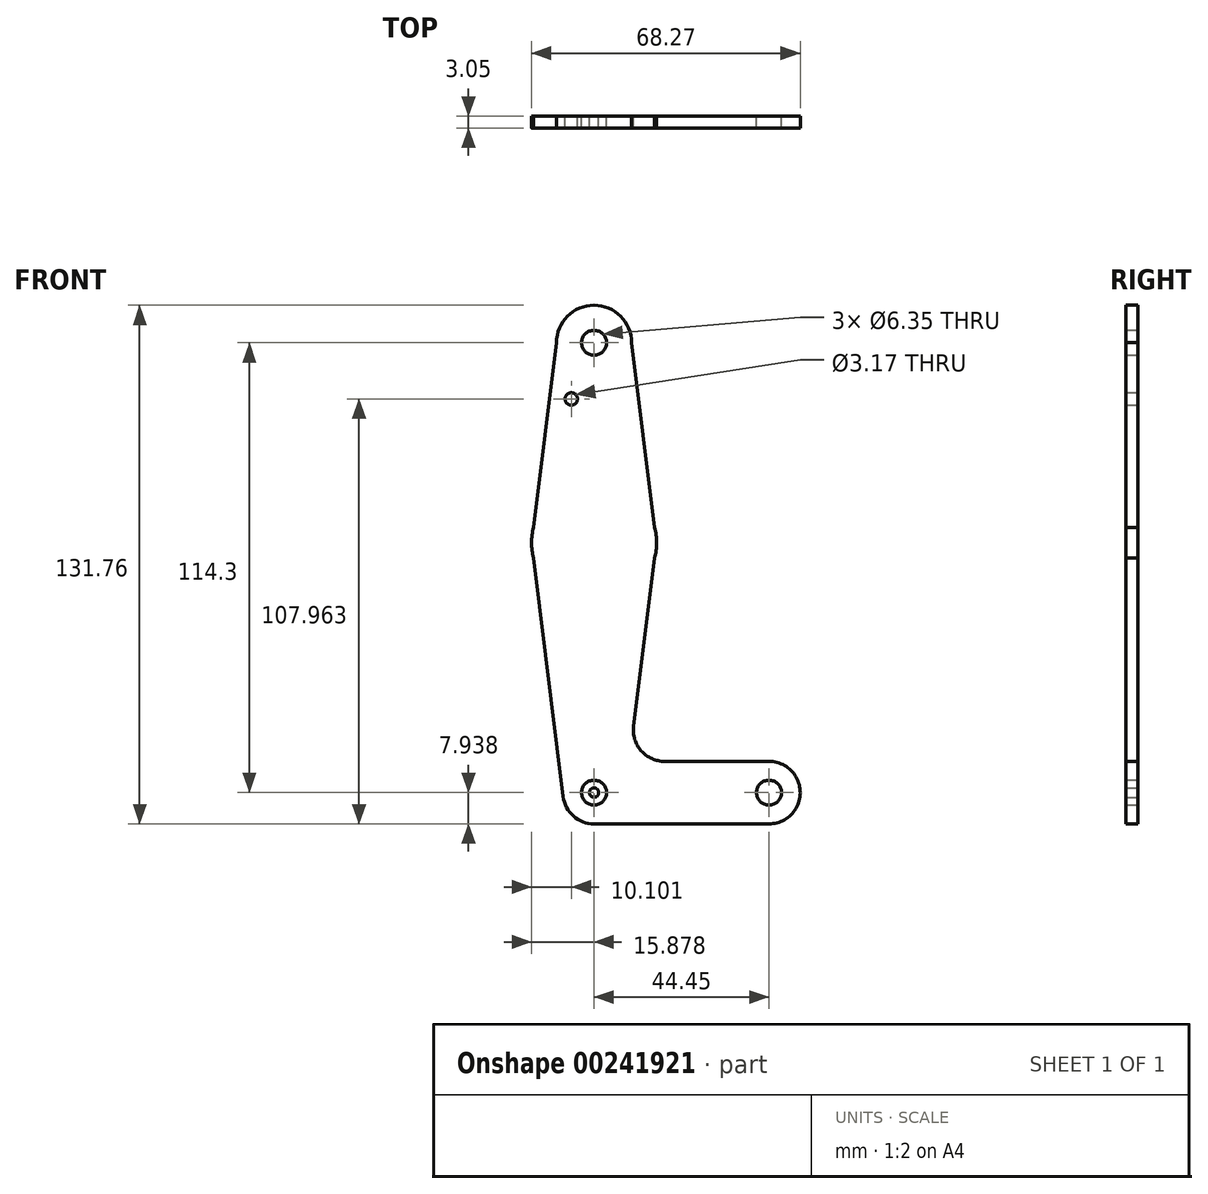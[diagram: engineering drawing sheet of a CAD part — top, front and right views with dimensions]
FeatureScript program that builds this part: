
annotation { "Feature Type Name" : "Feature", "Feature Type Description" : "" }
export const myFeature = defineFeature(function(context is Context, id is Id, definition is map)
    precondition{}
    {
        {
            var Q0;
            Q0=qCreatedBy(makeId("Front.planeOp"),FACE);
            var sketch = newSketch(context, id + "F0", { "sketchPlane" : qUnion([Q0])});
            skCircle(sketch, "E0", {"center": v(-26.22, 61.68) * mm, "radius": 9.53 * mm});
            skLineSegment(sketch, "E1", {"start": v(-26.22, 61.68) * mm, "end": v(-26.22, 10.88) * mm});
            skCircle(sketch, "E2", {"center": v(-26.22, 10.88) * mm, "radius": 15.88 * mm});
            skLineSegment(sketch, "E3", {"start": v(-26.22, 10.88) * mm, "end": v(-26.22, -52.62) * mm});
            skCircle(sketch, "E4", {"center": v(-26.22, -52.62) * mm, "radius": 7.94 * mm});
            skLineSegment(sketch, "E5", {"start": v(-26.22, -52.62) * mm, "end": v(18.23, -52.62) * mm});
            skCircle(sketch, "E6", {"center": v(18.23, -52.62) * mm, "radius": 7.94 * mm});
            skLineSegment(sketch, "E7", {"start": v(-42.1, 10.88) * mm, "end": v(-34.1, -53.6) * mm});
            skLineSegment(sketch, "E8", {"start": v(18.17, -60.56) * mm, "end": v(-26.22, -60.56) * mm});
            skLineSegment(sketch, "E9", {"start": v(-8.29, -44.68) * mm, "end": v(18.23, -44.68) * mm});
            skLineSegment(sketch, "E10", {"start": v(-26.22, 61.68) * mm, "end": v(-16.7, 61.68) * mm});
            skLineSegment(sketch, "E11", {"start": v(-16.7, 61.68) * mm, "end": v(-10.35, 10.88) * mm});
            skLineSegment(sketch, "E12", {"start": v(-42.1, 10.88) * mm, "end": v(-35.75, 61.68) * mm});
            skLineSegment(sketch, "E13", {"start": v(-10.35, 10.88) * mm, "end": v(-16.17, -35.75) * mm});
            skCircle(sketch, "E14", {"center": v(-26.22, 61.68) * mm, "radius": 3.18 * mm});
            skCircle(sketch, "E15", {"center": v(-32, 47.4) * mm, "radius": 1.59 * mm});
            skPoint(sketch, "E16.newPointB", {"position": v(-26.22, -44.68) * mm});
            skArc(sketch, "E16.filletArc", {"start": v(-16.17, -35.75) * mm, "mid": v(-14.25, -42) * mm, "end": v(-8.29, -44.68) * mm});
            skCircle(sketch, "E17", {"center": v(-26.22, -52.62) * mm, "radius": 3.18 * mm});
            skCircle(sketch, "E18", {"center": v(18.23, -52.62) * mm, "radius": 3.18 * mm});
            skCircle(sketch, "E19", {"center": v(-26.22, -52.62) * mm, "radius": 1.18 * mm});
            skSolve(sketch);
        }
        {
            var Q0;
            Q0 = qSketchRegion(id + "F0", true);
            var Q1;
            {var subQ0=sQuery(id+"F0.wireOp",EDGE,"E4");var subQ1=sQuery(id+"F0.wireOp",EDGE,"E3");var subQ2=makeQuery(id+"F0.imprint","INTERSECT",VERTEX,{"derivedFrom":[subQ1,subQ0]});Q1=makeQuery(id+"F0.imprint","IMPRINT",FACE,{"disambiguationData":[TD([[makeQuery(id+"F0.imprint","IMPRINT",EDGE,{"disambiguationData":[TD([[subQ2,-1.0]])],"derivedFrom":subQ1}),1.0]])]});}
            var Q2;
            {var subQ0=sQuery(id+"F0.wireOp",EDGE,"E5");var subQ1=sQuery(id+"F0.wireOp",EDGE,"E3");var subQ2=makeQuery(id+"F0.imprint","INTERSECT",VERTEX,{"derivedFrom":[subQ1,subQ0]});Q2=makeQuery(id+"F0.imprint","IMPRINT",FACE,{"disambiguationData":[TD([[makeQuery(id+"F0.imprint","IMPRINT",EDGE,{"disambiguationData":[TD([[subQ2,1.0]])],"derivedFrom":subQ1}),-1.0]])]});}
            var Q3;
            {var subQ0=sQuery(id+"F0.wireOp",EDGE,"E5");var subQ1=sQuery(id+"F0.wireOp",EDGE,"E3");var subQ2=makeQuery(id+"F0.imprint","INTERSECT",VERTEX,{"derivedFrom":[subQ1,subQ0]});Q3=makeQuery(id+"F0.imprint","IMPRINT",FACE,{"disambiguationData":[TD([[makeQuery(id+"F0.imprint","IMPRINT",EDGE,{"disambiguationData":[TD([[subQ2,1.0]])],"derivedFrom":subQ1}),1.0]])]});}
            extrude(context, id + "F1", {"entities" : qUnion([Q0, Q1, Q2, Q3]), "depth" : 3.05 * mm});
        }
    });
